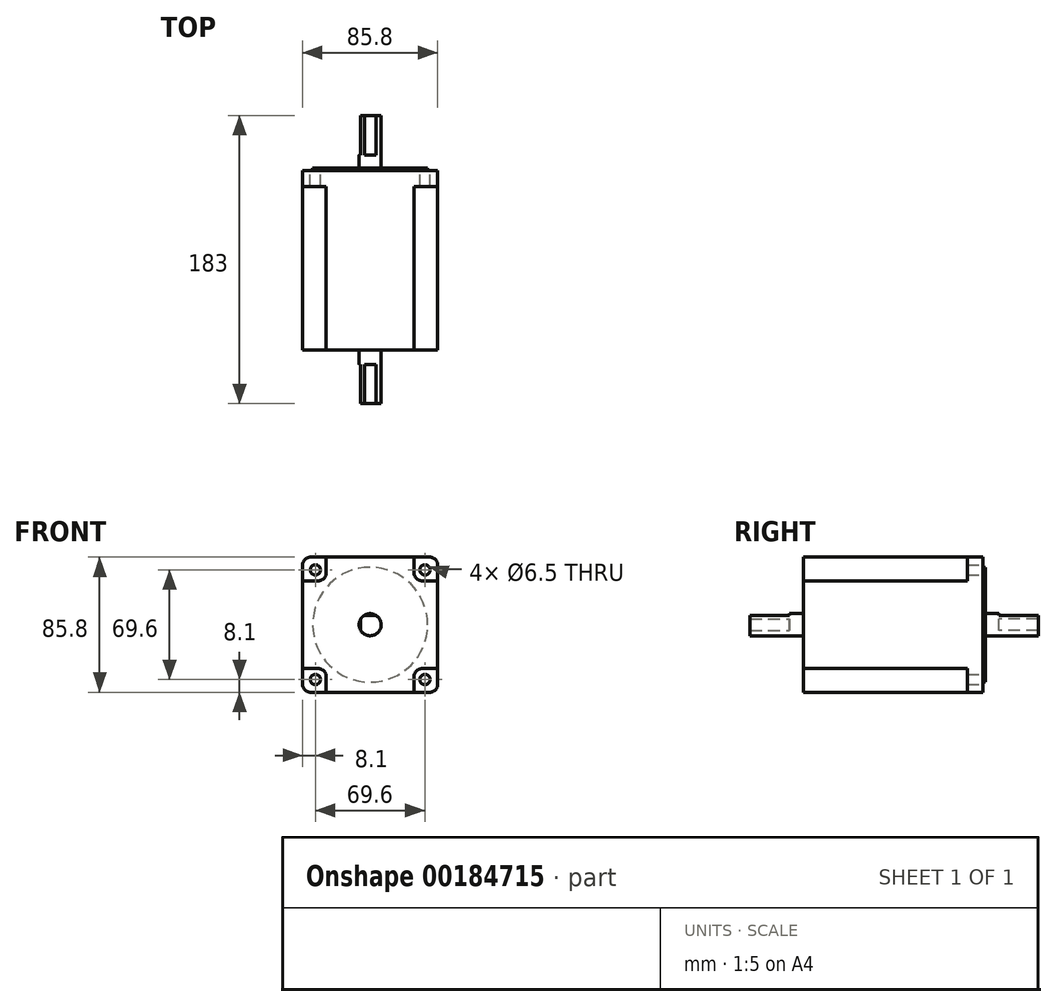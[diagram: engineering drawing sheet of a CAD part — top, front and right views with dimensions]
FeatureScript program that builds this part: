
annotation { "Feature Type Name" : "Feature", "Feature Type Description" : "" }
export const myFeature = defineFeature(function(context is Context, id is Id, definition is map)
    precondition{}
    {
        {
            var Q0;
            Q0=qCreatedBy(makeId("Front.planeOp"),FACE);
            var sketch = newSketch(context, id + "F0", { "sketchPlane" : qUnion([Q0])});
            skLineSegment(sketch, "E0.bottom", {"start": v(-37.9, 42.9) * mm, "end": v(37.9, 42.9) * mm});
            skLineSegment(sketch, "E0.top", {"start": v(-37.9, -42.9) * mm, "end": v(37.9, -42.9) * mm});
            skLineSegment(sketch, "E0.left", {"start": v(-42.9, 37.9) * mm, "end": v(-42.9, -37.9) * mm});
            skLineSegment(sketch, "E0.right", {"start": v(42.9, 37.9) * mm, "end": v(42.9, -37.9) * mm});
            skArc(sketch, "E1.filletArc", {"start": v(-42.9, -37.9) * mm, "mid": v(-41.44, -41.44) * mm, "end": v(-37.9, -42.9) * mm});
            skPoint(sketch, "E2.visualSharp", {"position": v(-42.9, 42.9) * mm});
            skArc(sketch, "E2.filletArc", {"start": v(-37.9, 42.9) * mm, "mid": v(-41.44, 41.44) * mm, "end": v(-42.9, 37.9) * mm});
            skPoint(sketch, "E3.visualSharp", {"position": v(42.9, 42.9) * mm});
            skArc(sketch, "E3.filletArc", {"start": v(42.9, 37.9) * mm, "mid": v(41.44, 41.44) * mm, "end": v(37.9, 42.9) * mm});
            skPoint(sketch, "E4.visualSharp", {"position": v(42.9, -42.9) * mm});
            skArc(sketch, "E4.filletArc", {"start": v(37.9, -42.9) * mm, "mid": v(41.44, -41.44) * mm, "end": v(42.9, -37.9) * mm});
            skSolve(sketch);
        }
        {
            var Q0;
            Q0=makeQuery(id+"F0.imprint","IMPRINT",FACE,{"disambiguationData":[TD([[makeQuery(id+"F0.imprint","IMPRINT",EDGE,{"derivedFrom":sQuery(id+"F0.wireOp",EDGE,"E0.bottom")}),-1.0]])]});
            extrude(context, id + "F1", {"entities" : qUnion([Q0]), "depth" : 114 * mm});
        }
        {
            var Q0;
            Q0=makeQuery(id+"F1.opExtrude","CAP_FACE",FACE,{"disambiguationData":[OSD([sQuery(id+"F0.wireOp",EDGE,"E0.bottom"),sQuery(id+"F0.wireOp",EDGE,"E0.top"),sQuery(id+"F0.wireOp",EDGE,"E0.left"),sQuery(id+"F0.wireOp",EDGE,"E0.right"),sQuery(id+"F0.wireOp",EDGE,"E1.filletArc"),sQuery(id+"F0.wireOp",EDGE,"E2.filletArc"),sQuery(id+"F0.wireOp",EDGE,"E3.filletArc"),sQuery(id+"F0.wireOp",EDGE,"E4.filletArc")])],"isStart":false});
            var sketch = newSketch(context, id + "F2", { "sketchPlane" : qUnion([Q0])});
            skLineSegment(sketch, "E5.bottom", {"start": v(27.9, 42.9) * mm, "end": v(42.9, 42.9) * mm});
            skLineSegment(sketch, "E5.top", {"start": v(27.9, 27.9) * mm, "end": v(42.9, 27.9) * mm});
            skLineSegment(sketch, "E5.left", {"start": v(27.9, 42.9) * mm, "end": v(27.9, 27.9) * mm});
            skLineSegment(sketch, "E5.right", {"start": v(42.9, 42.9) * mm, "end": v(42.9, 27.9) * mm});
            skLineSegment(sketch, "E6.MirrorCS", {"start": v(-27.9, 42.9) * mm, "end": v(-42.9, 42.9) * mm});
            skLineSegment(sketch, "E7.MirrorCS", {"start": v(-27.9, 27.9) * mm, "end": v(-42.9, 27.9) * mm});
            skLineSegment(sketch, "E8.MirrorCS", {"start": v(-42.9, 42.9) * mm, "end": v(-42.9, 27.9) * mm});
            skLineSegment(sketch, "E9.MirrorCS", {"start": v(-27.9, 42.9) * mm, "end": v(-27.9, 27.9) * mm});
            skLineSegment(sketch, "E10.MirrorCS", {"start": v(-27.9, -42.9) * mm, "end": v(-27.9, -27.9) * mm});
            skLineSegment(sketch, "E11.MirrorCS", {"start": v(-27.9, -42.9) * mm, "end": v(-42.9, -42.9) * mm});
            skLineSegment(sketch, "E12.MirrorCS", {"start": v(-27.9, -27.9) * mm, "end": v(-42.9, -27.9) * mm});
            skLineSegment(sketch, "E13.MirrorCS", {"start": v(-42.9, -42.9) * mm, "end": v(-42.9, -27.9) * mm});
            skLineSegment(sketch, "E14.MirrorCS", {"start": v(42.9, -42.9) * mm, "end": v(42.9, -27.9) * mm});
            skLineSegment(sketch, "E15.MirrorCS", {"start": v(27.9, -27.9) * mm, "end": v(42.9, -27.9) * mm});
            skLineSegment(sketch, "E16.MirrorCS", {"start": v(27.9, -42.9) * mm, "end": v(42.9, -42.9) * mm});
            skLineSegment(sketch, "E17.MirrorCS", {"start": v(27.9, -42.9) * mm, "end": v(27.9, -27.9) * mm});
            skSolve(sketch);
        }
        {
            var Q0;
            Q0=qSketchRegion(id+"F2",true);
            var Q1;
            Q1=makeQuery(id+"F1.opExtrude","CAP_FACE",FACE,{"disambiguationData":[OSD([sQuery(id+"F0.wireOp",EDGE,"E0.bottom"),sQuery(id+"F0.wireOp",EDGE,"E0.top"),sQuery(id+"F0.wireOp",EDGE,"E0.left"),sQuery(id+"F0.wireOp",EDGE,"E0.right"),sQuery(id+"F0.wireOp",EDGE,"E1.filletArc"),sQuery(id+"F0.wireOp",EDGE,"E2.filletArc"),sQuery(id+"F0.wireOp",EDGE,"E3.filletArc"),sQuery(id+"F0.wireOp",EDGE,"E4.filletArc")])],"isStart":false});
            extrude(context, id + "F3", {"entities" : qUnion([Q0]), "operationType" : NewBodyOperationType.REMOVE, "oppositeDirection" : true, "endBoundEntityFace" : qUnion([Q1]), "depth" : 104 * mm});
        }
        {
            var Q0;
            Q0=makeQuery(id+"F1.opExtrude","CAP_FACE",FACE,{"disambiguationData":[OSD([sQuery(id+"F0.wireOp",EDGE,"E0.bottom"),sQuery(id+"F0.wireOp",EDGE,"E0.top"),sQuery(id+"F0.wireOp",EDGE,"E0.left"),sQuery(id+"F0.wireOp",EDGE,"E0.right"),sQuery(id+"F0.wireOp",EDGE,"E1.filletArc"),sQuery(id+"F0.wireOp",EDGE,"E2.filletArc"),sQuery(id+"F0.wireOp",EDGE,"E3.filletArc"),sQuery(id+"F0.wireOp",EDGE,"E4.filletArc")])],"isStart":true});
            var sketch = newSketch(context, id + "F4", { "sketchPlane" : qUnion([Q0])});
            skCircle(sketch, "E18", {"center": v(34.8, 34.8) * mm, "radius": 3.25 * mm});
            skCircle(sketch, "E19.MirrorC", {"center": v(-34.8, 34.8) * mm, "radius": 3.25 * mm});
            skCircle(sketch, "E20.MirrorC", {"center": v(34.8, -34.8) * mm, "radius": 3.25 * mm});
            skCircle(sketch, "E21.MirrorC", {"center": v(-34.8, -34.8) * mm, "radius": 3.25 * mm});
            skSolve(sketch);
        }
        {
            var Q0;
            Q0=qSketchRegion(id+"F4",true);
            extrude(context, id + "F5", {"entities" : qUnion([Q0]), "operationType" : NewBodyOperationType.REMOVE, "endBound" : BoundingType.UP_TO_NEXT, "oppositeDirection" : true, "depth" : 25 * mm});
        }
        {
            var Q0;
            Q0=makeQuery(id+"F3.boolean.opBoolean","COPY",EDGE,{"derivedFrom":makeQuery(id+"F3.opExtrude","SWEPT_EDGE",EDGE,{"disambiguationData":[OSD([sQuery(id+"F0.wireOp",EDGE,"E0.left"),sQuery(id+"F2.wireOp",EDGE,"E8.MirrorCS"),sQuery(id+"F2.wireOp",EDGE,"E7.MirrorCS")])]})});
            var Q1;
            Q1=makeQuery(id+"F3.boolean.opBoolean","COPY",EDGE,{"derivedFrom":makeQuery(id+"F3.opExtrude","SWEPT_EDGE",EDGE,{"disambiguationData":[OSD([sQuery(id+"F0.wireOp",EDGE,"E0.left"),sQuery(id+"F2.wireOp",EDGE,"E13.MirrorCS"),sQuery(id+"F2.wireOp",EDGE,"E12.MirrorCS")])]})});
            var Q2;
            Q2=makeQuery(id+"F3.boolean.opBoolean","COPY",EDGE,{"derivedFrom":makeQuery(id+"F3.opExtrude","SWEPT_EDGE",EDGE,{"disambiguationData":[OSD([sQuery(id+"F2.wireOp",EDGE,"E12.MirrorCS"),sQuery(id+"F2.wireOp",EDGE,"E10.MirrorCS")])]})});
            var Q3;
            Q3=makeQuery(id+"F3.boolean.opBoolean","COPY",EDGE,{"derivedFrom":makeQuery(id+"F3.opExtrude","SWEPT_EDGE",EDGE,{"disambiguationData":[OSD([sQuery(id+"F0.wireOp",EDGE,"E0.top"),sQuery(id+"F2.wireOp",EDGE,"E10.MirrorCS"),sQuery(id+"F2.wireOp",EDGE,"E11.MirrorCS")])]})});
            var Q4;
            Q4=makeQuery(id+"F3.boolean.opBoolean","COPY",EDGE,{"derivedFrom":makeQuery(id+"F3.opExtrude","SWEPT_EDGE",EDGE,{"disambiguationData":[OSD([sQuery(id+"F0.wireOp",EDGE,"E0.top"),sQuery(id+"F2.wireOp",EDGE,"E17.MirrorCS"),sQuery(id+"F2.wireOp",EDGE,"E16.MirrorCS")])]})});
            var Q5;
            Q5=makeQuery(id+"F3.boolean.opBoolean","COPY",EDGE,{"derivedFrom":makeQuery(id+"F3.opExtrude","SWEPT_EDGE",EDGE,{"disambiguationData":[OSD([sQuery(id+"F0.wireOp",EDGE,"E0.bottom"),sQuery(id+"F2.wireOp",EDGE,"E9.MirrorCS"),sQuery(id+"F2.wireOp",EDGE,"E6.MirrorCS")])]})});
            var Q6;
            Q6=makeQuery(id+"F3.boolean.opBoolean","COPY",EDGE,{"derivedFrom":makeQuery(id+"F3.opExtrude","SWEPT_EDGE",EDGE,{"disambiguationData":[OSD([sQuery(id+"F2.wireOp",EDGE,"E17.MirrorCS"),sQuery(id+"F2.wireOp",EDGE,"E15.MirrorCS")])]})});
            var Q7;
            Q7=makeQuery(id+"F3.boolean.opBoolean","COPY",EDGE,{"derivedFrom":makeQuery(id+"F3.opExtrude","SWEPT_EDGE",EDGE,{"disambiguationData":[OSD([sQuery(id+"F0.wireOp",EDGE,"E0.right"),sQuery(id+"F2.wireOp",EDGE,"E14.MirrorCS"),sQuery(id+"F2.wireOp",EDGE,"E15.MirrorCS")])]})});
            var Q8;
            Q8=makeQuery(id+"F3.boolean.opBoolean","COPY",EDGE,{"derivedFrom":makeQuery(id+"F3.opExtrude","SWEPT_EDGE",EDGE,{"disambiguationData":[OSD([sQuery(id+"F0.wireOp",EDGE,"E0.right"),sQuery(id+"F2.wireOp",EDGE,"E5.right"),sQuery(id+"F2.wireOp",EDGE,"E5.top")])]})});
            var Q9;
            Q9=makeQuery(id+"F3.boolean.opBoolean","COPY",EDGE,{"derivedFrom":makeQuery(id+"F3.opExtrude","SWEPT_EDGE",EDGE,{"disambiguationData":[OSD([sQuery(id+"F0.wireOp",EDGE,"E0.bottom"),sQuery(id+"F2.wireOp",EDGE,"E5.bottom"),sQuery(id+"F2.wireOp",EDGE,"E5.left")])]})});
            var Q10;
            Q10=makeQuery(id+"F3.boolean.opBoolean","COPY",EDGE,{"derivedFrom":makeQuery(id+"F3.opExtrude","SWEPT_EDGE",EDGE,{"disambiguationData":[OSD([sQuery(id+"F2.wireOp",EDGE,"E5.top"),sQuery(id+"F2.wireOp",EDGE,"E5.left")])]})});
            var Q11;
            Q11=makeQuery(id+"F3.boolean.opBoolean","COPY",EDGE,{"derivedFrom":makeQuery(id+"F3.opExtrude","SWEPT_EDGE",EDGE,{"disambiguationData":[OSD([sQuery(id+"F2.wireOp",EDGE,"E9.MirrorCS"),sQuery(id+"F2.wireOp",EDGE,"E7.MirrorCS")])]})});
            fillet(context, id + "F6", {"entities" : qUnion([Q0, Q1, Q2, Q3, Q4, Q5, Q6, Q7, Q8, Q9, Q10, Q11]), "radius" : 5 * mm, "tangentPropagation" : true, "allowEdgeOverflow" : false});
        }
        {
            var Q0;
            Q0=makeQuery(id+"F1.opExtrude","CAP_FACE",FACE,{"disambiguationData":[OSD([sQuery(id+"F0.wireOp",EDGE,"E0.bottom"),sQuery(id+"F0.wireOp",EDGE,"E0.top"),sQuery(id+"F0.wireOp",EDGE,"E0.left"),sQuery(id+"F0.wireOp",EDGE,"E0.right"),sQuery(id+"F0.wireOp",EDGE,"E1.filletArc"),sQuery(id+"F0.wireOp",EDGE,"E2.filletArc"),sQuery(id+"F0.wireOp",EDGE,"E3.filletArc"),sQuery(id+"F0.wireOp",EDGE,"E4.filletArc")])],"isStart":true});
            var sketch = newSketch(context, id + "F7", { "sketchPlane" : qUnion([Q0])});
            skCircle(sketch, "E22", {"center": v(0, 0) * mm, "radius": 36.5 * mm});
            skSolve(sketch);
        }
        {
            var Q0;
            Q0=qSketchRegion(id+"F7",true);
            extrude(context, id + "F8", {"entities" : qUnion([Q0]), "operationType" : NewBodyOperationType.ADD, "depth" : 1.6 * mm});
        }
        {
            var Q0;
            Q0=makeQuery(id+"F1.opExtrude","CAP_FACE",FACE,{"disambiguationData":[OSD([sQuery(id+"F0.wireOp",EDGE,"E0.bottom"),sQuery(id+"F0.wireOp",EDGE,"E0.top"),sQuery(id+"F0.wireOp",EDGE,"E0.left"),sQuery(id+"F0.wireOp",EDGE,"E0.right"),sQuery(id+"F0.wireOp",EDGE,"E1.filletArc"),sQuery(id+"F0.wireOp",EDGE,"E2.filletArc"),sQuery(id+"F0.wireOp",EDGE,"E3.filletArc"),sQuery(id+"F0.wireOp",EDGE,"E4.filletArc")])],"isStart":true});
            var sketch = newSketch(context, id + "F9", { "sketchPlane" : qUnion([Q0])});
            skCircle(sketch, "E23", {"center": v(0, 0) * mm, "radius": 7 * mm});
            skSolve(sketch);
        }
        {
            var Q0;
            Q0=qSketchRegion(id+"F9",true);
            var Q1;
            Q1=sQuery(id+"F9.wireOp",EDGE,"E23");
            extrude(context, id + "F10", {"entities" : qUnion([Q0]), "operationType" : NewBodyOperationType.ADD, "surfaceEntities" : qUnion([Q1]), "depth" : 35 * mm});
        }
        {
            var Q0;
            Q0=makeQuery(id+"F10.opExtrude","CAP_FACE",FACE,{"disambiguationData":[OSD([sQuery(id+"F9.wireOp",EDGE,"E23")])],"isStart":false});
            var sketch = newSketch(context, id + "F11", { "sketchPlane" : qUnion([Q0])});
            skLineSegment(sketch, "E24", {"start": v(-14.54, 6) * mm, "end": v(6, 6) * mm});
            skLineSegment(sketch, "E25", {"start": v(6, -12.05) * mm, "end": v(6, 6) * mm});
            skLineSegment(sketch, "E26", {"start": v(-14.54, 6) * mm, "end": v(-14.54, 12.76) * mm});
            skLineSegment(sketch, "E27", {"start": v(-14.54, 12.76) * mm, "end": v(13.2, 12.76) * mm});
            skLineSegment(sketch, "E28", {"start": v(13.2, 12.76) * mm, "end": v(13.2, -12.47) * mm});
            skLineSegment(sketch, "E29", {"start": v(13.2, -12.47) * mm, "end": v(6, -12.05) * mm});
            skSolve(sketch);
        }
        {
            var Q0;
            Q0 = qSketchRegion(id + "F11", true);
            extrude(context, id + "F12", {"entities" : qUnion([Q0]), "operationType" : NewBodyOperationType.REMOVE, "oppositeDirection" : true, "depth" : 25 * mm});
        }
        {
            var Q0;
            Q0=makeQuery(id+"F1.opExtrude","CAP_FACE",FACE,{"disambiguationData":[OSD([sQuery(id+"F0.wireOp",EDGE,"E0.bottom"),sQuery(id+"F0.wireOp",EDGE,"E0.top"),sQuery(id+"F0.wireOp",EDGE,"E0.left"),sQuery(id+"F0.wireOp",EDGE,"E0.right"),sQuery(id+"F0.wireOp",EDGE,"E1.filletArc"),sQuery(id+"F0.wireOp",EDGE,"E2.filletArc"),sQuery(id+"F0.wireOp",EDGE,"E3.filletArc"),sQuery(id+"F0.wireOp",EDGE,"E4.filletArc")])],"isStart":false});
            var sketch = newSketch(context, id + "F13", { "sketchPlane" : qUnion([Q0])});
            skCircle(sketch, "E30", {"center": v(0, 0) * mm, "radius": 7 * mm});
            skSolve(sketch);
        }
        {
            var Q0;
            Q0 = qSketchRegion(id + "F13", true);
            extrude(context, id + "F14", {"entities" : qUnion([Q0]), "operationType" : NewBodyOperationType.ADD, "depth" : 34 * mm});
        }
        {
            var Q0;
            Q0=makeQuery(id+"F14.opExtrude","CAP_FACE",FACE,{"disambiguationData":[OSD([sQuery(id+"F13.wireOp",EDGE,"E30")])],"isStart":false});
            var sketch = newSketch(context, id + "F15", { "sketchPlane" : qUnion([Q0])});
            skLineSegment(sketch, "E31", {"start": v(-6, 6) * mm, "end": v(6, 6) * mm});
            skLineSegment(sketch, "E32", {"start": v(-6, -11.15) * mm, "end": v(-6, 6) * mm});
            skLineSegment(sketch, "E33", {"start": v(-6, -11.15) * mm, "end": v(-11.24, 11.01) * mm});
            skLineSegment(sketch, "E34", {"start": v(-11.24, 11.01) * mm, "end": v(6, 6) * mm});
            skSolve(sketch);
        }
        {
            var Q0;
            Q0 = qSketchRegion(id + "F15", true);
            extrude(context, id + "F16", {"entities" : qUnion([Q0]), "operationType" : NewBodyOperationType.REMOVE, "oppositeDirection" : true, "depth" : 25 * mm});
        }
    });
